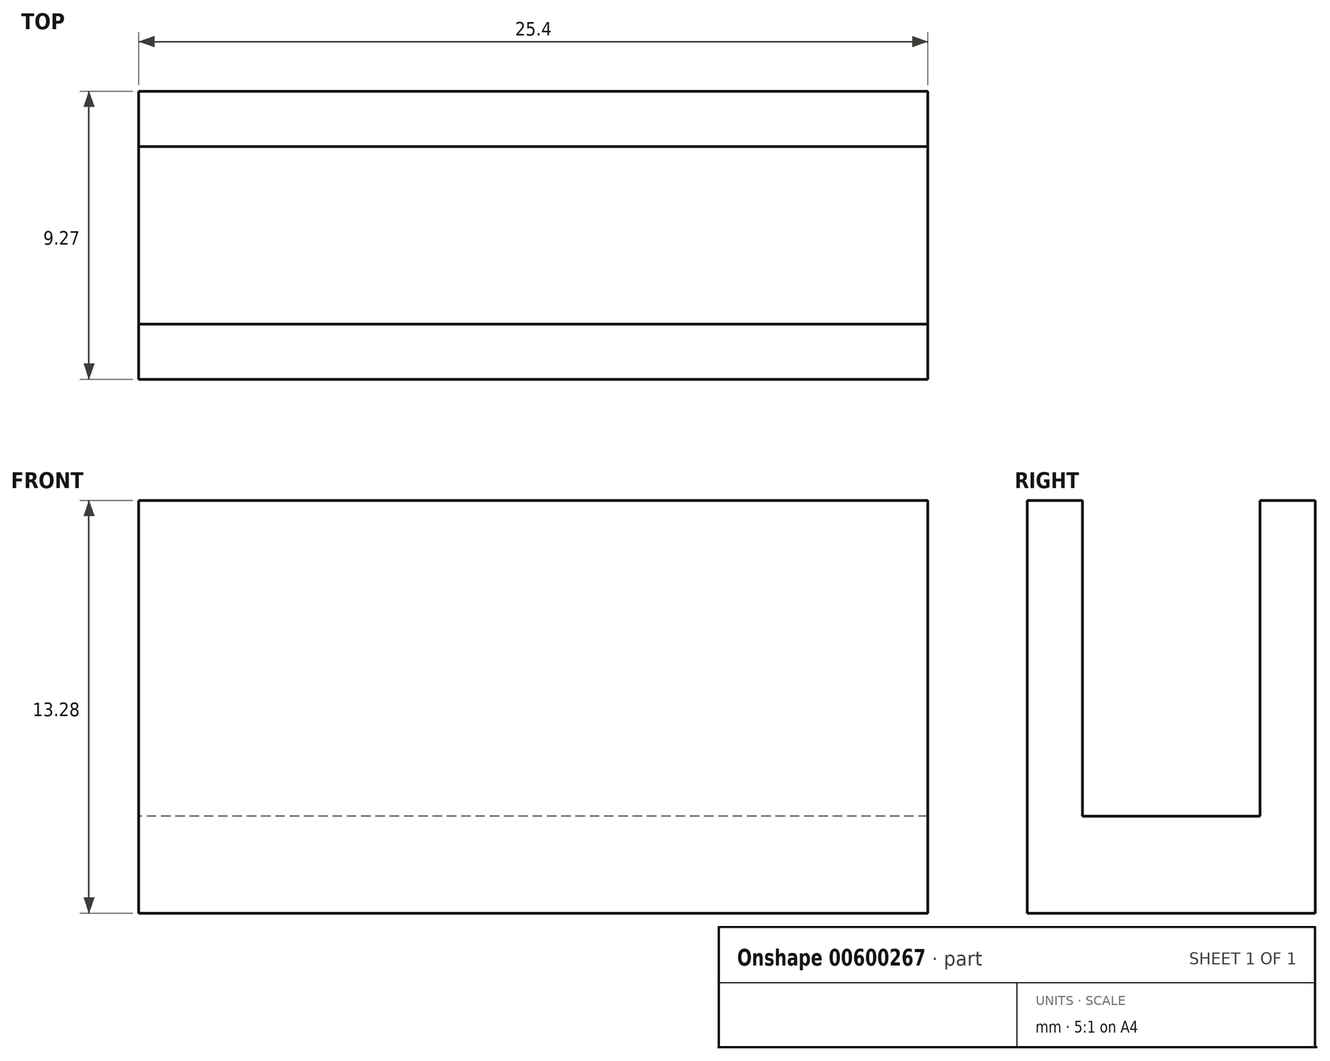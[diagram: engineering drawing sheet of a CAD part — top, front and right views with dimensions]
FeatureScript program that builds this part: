
annotation { "Feature Type Name" : "Feature", "Feature Type Description" : "" }
export const myFeature = defineFeature(function(context is Context, id is Id, definition is map)
    precondition{}
    {
        {
            var Q0;
            Q0=qCreatedBy(makeId("Top.planeOp"),FACE);
            var sketch = newSketch(context, id + "F0", { "sketchPlane" : qUnion([Q0])});
            skLineSegment(sketch, "E0.bottom", {"start": v(0, 0) * mm, "end": v(25.4, 0) * mm});
            skLineSegment(sketch, "E0.top", {"start": v(0, -9.27) * mm, "end": v(25.4, -9.27) * mm});
            skLineSegment(sketch, "E0.left", {"start": v(0, 0) * mm, "end": v(0, -9.27) * mm});
            skLineSegment(sketch, "E0.right", {"start": v(25.4, 0) * mm, "end": v(25.4, -9.27) * mm});
            skSolve(sketch);
        }
        {
            var Q0;
            Q0=qSketchRegion(id+"F0",true);
            extrude(context, id + "F1", {"entities" : qUnion([Q0]), "depth" : 3.12 * mm, "offsetDistance" : 25.4 * mm});
        }
        {
            var Q0;
            Q0=makeQuery(id+"F1.opExtrude","CAP_FACE",FACE,{"disambiguationData":[OSD([sQuery(id+"F0.wireOp",EDGE,"E0.bottom"),sQuery(id+"F0.wireOp",EDGE,"E0.top"),sQuery(id+"F0.wireOp",EDGE,"E0.left"),sQuery(id+"F0.wireOp",EDGE,"E0.right")])],"isStart":false});
            var sketch = newSketch(context, id + "F2", { "sketchPlane" : qUnion([Q0])});
            skLineSegment(sketch, "E1.bottom", {"start": v(0, 0) * mm, "end": v(25.4, 0) * mm});
            skLineSegment(sketch, "E1.top", {"start": v(0, -1.78) * mm, "end": v(25.4, -1.78) * mm});
            skLineSegment(sketch, "E1.left", {"start": v(0, 0) * mm, "end": v(0, -1.78) * mm});
            skLineSegment(sketch, "E1.right", {"start": v(25.4, 0) * mm, "end": v(25.4, -1.78) * mm});
            skLineSegment(sketch, "E2.bottom", {"start": v(25.4, -9.27) * mm, "end": v(0, -9.27) * mm});
            skLineSegment(sketch, "E2.top", {"start": v(25.4, -7.5) * mm, "end": v(0, -7.5) * mm});
            skLineSegment(sketch, "E2.left", {"start": v(25.4, -9.27) * mm, "end": v(25.4, -7.5) * mm});
            skLineSegment(sketch, "E2.right", {"start": v(0, -9.27) * mm, "end": v(0, -7.5) * mm});
            skSolve(sketch);
        }
        {
            var Q0;
            Q0=qSketchRegion(id+"F2",true);
            extrude(context, id + "F3", {"entities" : qUnion([Q0]), "operationType" : NewBodyOperationType.ADD, "depth" : 10.16 * mm, "offsetDistance" : 25.4 * mm});
        }
    });
